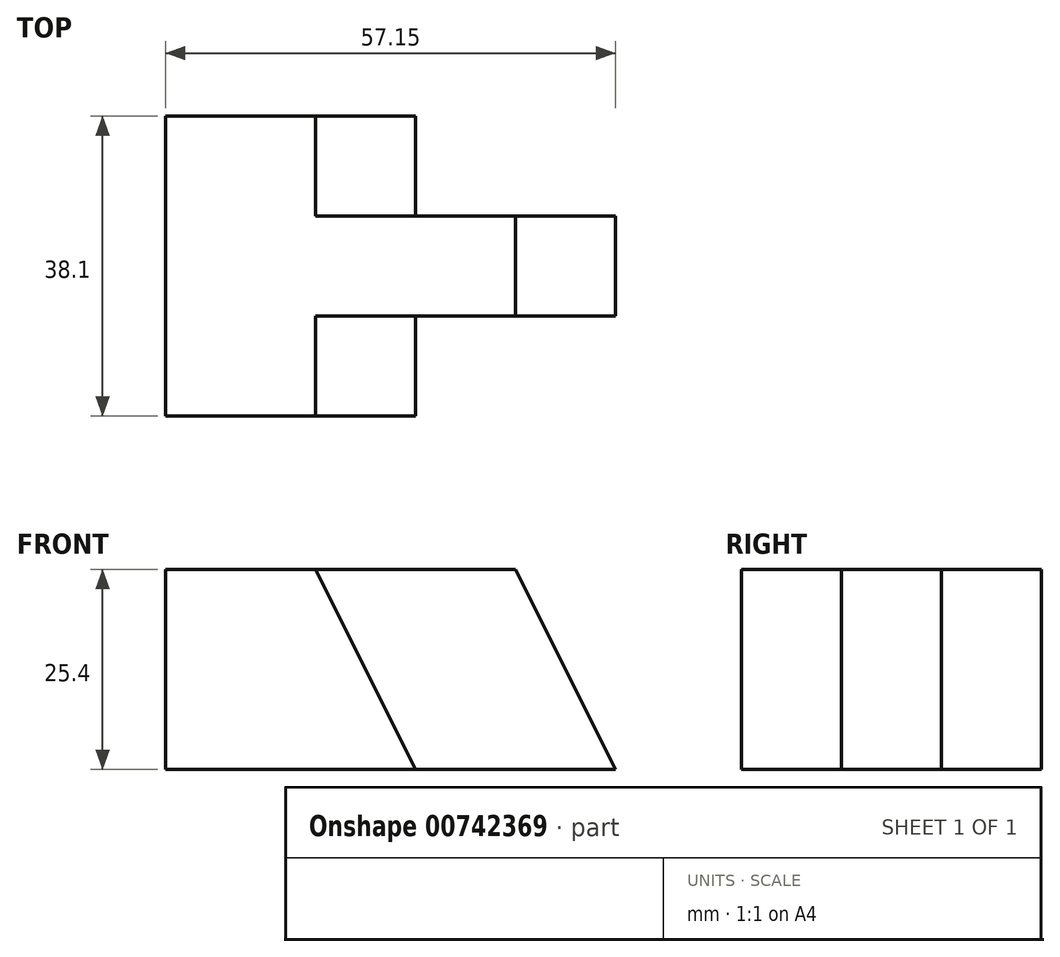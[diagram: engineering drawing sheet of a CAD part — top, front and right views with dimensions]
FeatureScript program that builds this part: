
annotation { "Feature Type Name" : "Feature", "Feature Type Description" : "" }
export const myFeature = defineFeature(function(context is Context, id is Id, definition is map)
    precondition{}
    {
        {
            var Q0;
            Q0=qCreatedBy(makeId("Front.planeOp"),FACE);
            var sketch = newSketch(context, id + "F0", { "sketchPlane" : qUnion([Q0])});
            skLineSegment(sketch, "E0.bottom", {"start": v(0, 0) * mm, "end": v(-57.15, 0) * mm});
            skLineSegment(sketch, "E0.top", {"start": v(0, 25.4) * mm, "end": v(-57.15, 25.4) * mm});
            skLineSegment(sketch, "E0.left", {"start": v(0, 0) * mm, "end": v(0, 25.4) * mm});
            skLineSegment(sketch, "E0.right", {"start": v(-57.15, 0) * mm, "end": v(-57.15, 25.4) * mm});
            skSolve(sketch);
        }
        {
            var Q0;
            Q0 = qSketchRegion(id + "F0", true);
            extrude(context, id + "F1", {"entities" : qUnion([Q0]), "depth" : 38.1 * mm, "offsetDistance" : 25.4 * mm});
        }
        {
            var Q0;
            Q0=makeQuery(id+"F1.opExtrude","CAP_FACE",FACE,{"disambiguationData":[OSD([sQuery(id+"F0.wireOp",EDGE,"E0.bottom"),sQuery(id+"F0.wireOp",EDGE,"E0.top"),sQuery(id+"F0.wireOp",EDGE,"E0.left"),sQuery(id+"F0.wireOp",EDGE,"E0.right")])],"isStart":false});
            var sketch = newSketch(context, id + "F2", { "sketchPlane" : qUnion([Q0])});
            skLineSegment(sketch, "E1", {"start": v(0, 0) * mm, "end": v(-12.7, 25.4) * mm});
            skLineSegment(sketch, "E2", {"start": v(-12.7, 25.4) * mm, "end": v(-38.1, 25.4) * mm});
            skLineSegment(sketch, "E3", {"start": v(-38.1, 25.4) * mm, "end": v(-25.4, 0) * mm});
            skLineSegment(sketch, "E4", {"start": v(-25.4, 0) * mm, "end": v(0, 0) * mm});
            skLineSegment(sketch, "E5", {"start": v(0, 0) * mm, "end": v(-25.4, 0) * mm});
            skSolve(sketch);
        }
        {
            var Q0;
            {var subQ0=sQuery(id+"F2.wireOp",EDGE,"E1");Q0=makeQuery(id+"F2.imprint","IMPRINT",FACE,{"disambiguationData":[TD([[makeQuery(id+"F2.imprint","IMPRINT",EDGE,{"derivedFrom":subQ0}),-1.0]])]});}
            extrude(context, id + "F3", {"entities" : qUnion([Q0]), "operationType" : NewBodyOperationType.REMOVE, "endBound" : BoundingType.THROUGH_ALL, "oppositeDirection" : true, "depth" : 25.4 * mm, "offsetDistance" : 25.4 * mm});
        }
        {
            var Q0;
            Q0=makeQuery(id+"F1.opExtrude","CAP_FACE",FACE,{"disambiguationData":[OSD([sQuery(id+"F0.wireOp",EDGE,"E0.bottom"),sQuery(id+"F0.wireOp",EDGE,"E0.top"),sQuery(id+"F0.wireOp",EDGE,"E0.left"),sQuery(id+"F0.wireOp",EDGE,"E0.right")])],"isStart":false});
            var sketch = newSketch(context, id + "F4", { "sketchPlane" : qUnion([Q0])});
            skLineSegment(sketch, "E6", {"start": v(-38.1, 25.4) * mm, "end": v(-25.4, 0) * mm});
            skSolve(sketch);
        }
        {
            var Q0;
            {var subQ0=sQuery(id+"F4.wireOp",EDGE,"E6");Q0=makeQuery(id+"F4.imprint","IMPRINT",FACE,{"disambiguationData":[TD([[makeQuery(id+"F4.imprint","IMPRINT",EDGE,{"derivedFrom":subQ0}),1.0]])]});}
            extrude(context, id + "F5", {"entities" : qUnion([Q0]), "operationType" : NewBodyOperationType.REMOVE, "oppositeDirection" : true, "depth" : 12.7 * mm, "offsetDistance" : 25.4 * mm});
        }
        {
            var Q0;
            Q0=makeQuery(id+"F1.opExtrude","CAP_FACE",FACE,{"disambiguationData":[OSD([sQuery(id+"F0.wireOp",EDGE,"E0.bottom"),sQuery(id+"F0.wireOp",EDGE,"E0.top"),sQuery(id+"F0.wireOp",EDGE,"E0.left"),sQuery(id+"F0.wireOp",EDGE,"E0.right")])],"isStart":true});
            var sketch = newSketch(context, id + "F6", { "sketchPlane" : qUnion([Q0])});
            skLineSegment(sketch, "E7", {"start": v(38.1, 25.4) * mm, "end": v(25.4, 0) * mm});
            skSolve(sketch);
        }
        {
            var Q0;
            {var subQ0=sQuery(id+"F6.wireOp",EDGE,"E7");Q0=makeQuery(id+"F6.imprint","IMPRINT",FACE,{"disambiguationData":[TD([[makeQuery(id+"F6.imprint","IMPRINT",EDGE,{"derivedFrom":subQ0}),-1.0]])]});}
            extrude(context, id + "F7", {"entities" : qUnion([Q0]), "operationType" : NewBodyOperationType.REMOVE, "oppositeDirection" : true, "depth" : 12.7 * mm, "offsetDistance" : 25.4 * mm});
        }
    });
